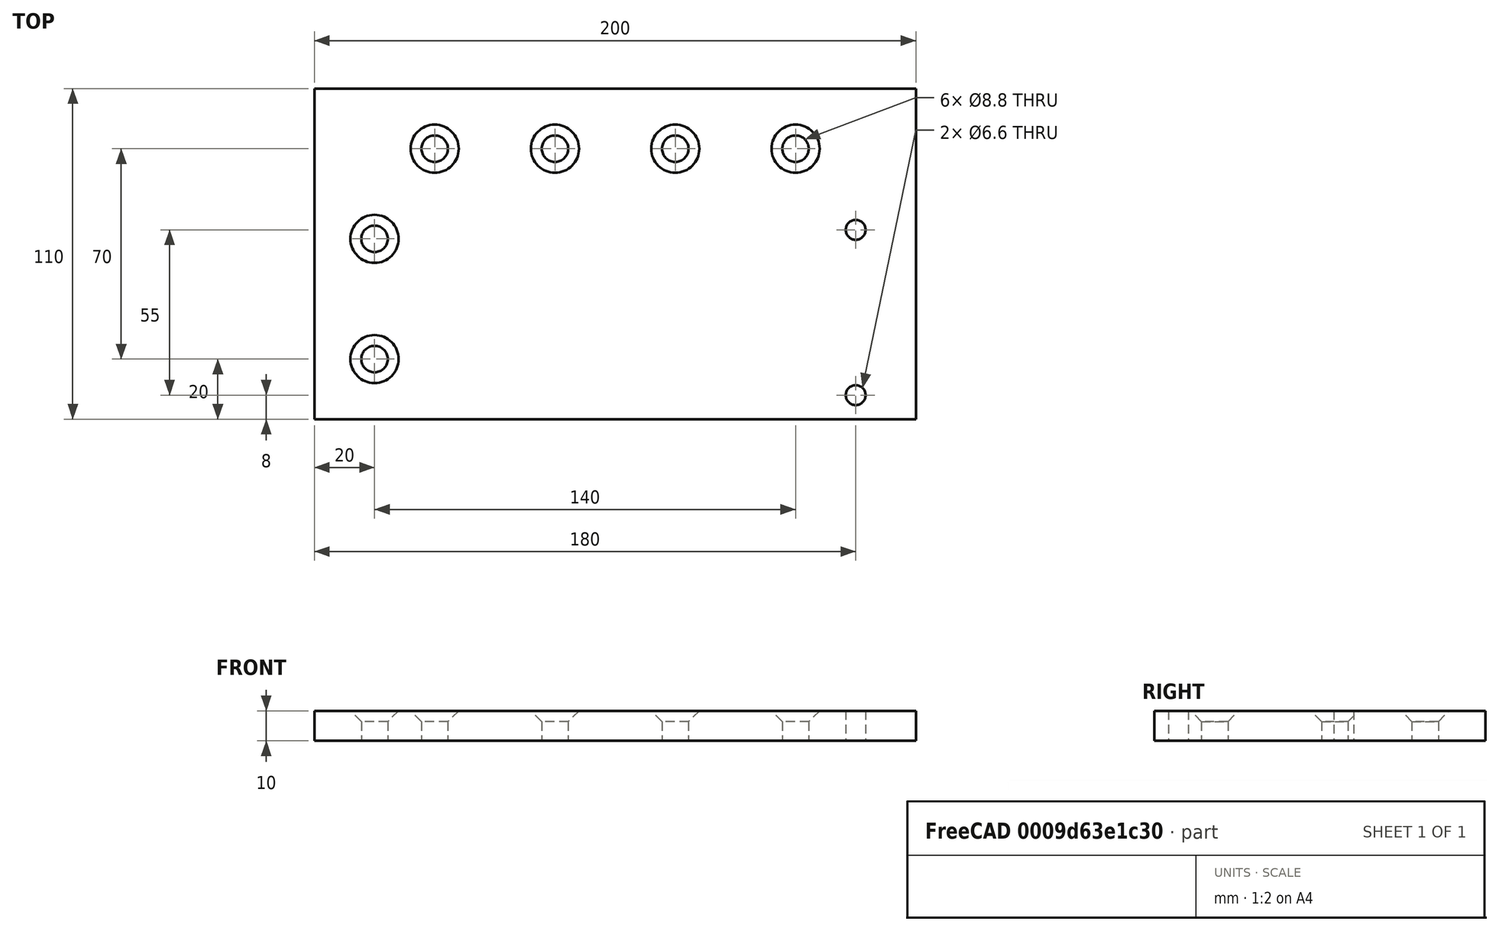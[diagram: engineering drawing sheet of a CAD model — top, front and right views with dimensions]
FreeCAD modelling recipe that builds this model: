
FCSTD DOCUMENT  (FreeCAD 0.17R13528 (Git))
Label: plate4
License: All rights reserved
LicenseURL: http://en.wikipedia.org/wiki/All_rights_reserved
objects: TechDraw::DrawViewDimension×22, Sketcher::SketchObject×4, PartDesign::Hole×3, PartDesign::LinearPattern×3, TechDraw::DrawProjGroupItem×3, PartDesign::Pad×1, PartDesign::Body×1, TechDraw::DrawSVGTemplate×1, TechDraw::DrawProjGroup×1, TechDraw::DrawViewAnnotation×1, TechDraw::DrawPage×1
note: 16 computed .brp shape members not serialized (recipe doc carries the construction recipe); baked Part::Feature solids carry a one-line shape summary decoded from their .brp

FEATURE [Sketcher::SketchObject] Sketch
  MapMode = 5
  Support = -> [XY_Plane]
  sketch-geometry (4):
    g0: LineSegment StartX=0 StartY=0 StartZ=0 EndX=200 EndY=0 EndZ=0
    g1: LineSegment StartX=200 StartY=0 StartZ=0 EndX=200 EndY=110 EndZ=0
    g2: LineSegment StartX=200 StartY=110 StartZ=0 EndX=0 EndY=110 EndZ=0
    g3: LineSegment StartX=0 StartY=110 StartZ=0 EndX=0 EndY=0 EndZ=0
  constraints (11):
    c: Coincident(g0,g1)
    c: Coincident(g1,g2)
    c: Coincident(g2,g3)
    c: Coincident(g3,g0)
    c: Horizontal(g0)
    c: Horizontal(g2)
    c: Vertical(g1)
    c: Vertical(g3)
    c: Coincident(g0,g-1)
    c: DistanceX(g0,g0) = 200
    c: DistanceY(g3,g3) = 110
FEATURE [PartDesign::Pad] Pad
  Length = 10
  Length2 = 100
  Profile = -> Sketch
  Type = 0
FEATURE [Sketcher::SketchObject] Sketch001
  MapMode = 5
  Placement = pos=(0,0,10) rot=(0,0,1;0rad)
  Support = -> [Pad]
  sketch-geometry (1):
    g0: Circle CenterX=20 CenterY=20 CenterZ=0 NormalX=0 NormalY=0 NormalZ=1 AngleXU=0 Radius=6.68651
  constraints (2):
    c: Distance(g0,g-1) = 20
    c: Distance(g0,g-2) = 20
FEATURE [PartDesign::Hole] Hole
  BaseFeature = -> Pad
  Depth = 25
  DepthType = 1
  Diameter = 8.8
  DrillPoint = 0
  DrillPointAngle = 118
  HoleCutCountersinkAngle = 90
  HoleCutDepth = 0
  HoleCutDiameter = 16
  HoleCutType = 2
  ModelActualThread = false
  Profile = -> Sketch001
  Tapered = false
  TaperedAngle = 90
  ThreadAngle = 0
  ThreadClass = 0
  ThreadCutOffInner = 0
  ThreadCutOffOuter = 0
  ThreadDirection = 0
  ThreadFit = 0
  ThreadPitch = 0
  ThreadSize = 8
  ThreadType = 1
  Threaded = false
FEATURE [PartDesign::LinearPattern] LinearPattern
  BaseFeature = -> Hole
  Direction = -> Sketch001 [V_Axis]
  Length = 40
  Occurrences = 2
  Originals = -> [Hole]
FEATURE [Sketcher::SketchObject] Sketch002
  MapMode = 5
  Placement = pos=(0,0,10) rot=(0,0,1;0rad)
  sketch-geometry (1):
    g0: Circle CenterX=180 CenterY=63 CenterZ=0 NormalX=0 NormalY=0 NormalZ=1 AngleXU=0 Radius=8.06203
  constraints (2):
    c: Distance(g0,g-1) = 63
    c: Distance(g0,g-2) = 180
FEATURE [PartDesign::Hole] Hole001
  BaseFeature = -> LinearPattern
  Depth = 25
  DepthType = 1
  Diameter = 6.6
  DrillPoint = 0
  DrillPointAngle = 118
  HoleCutCountersinkAngle = 90
  HoleCutDepth = 0
  HoleCutDiameter = 6
  HoleCutType = 0
  ModelActualThread = false
  Profile = -> Sketch002
  Tapered = false
  TaperedAngle = 90
  ThreadAngle = 60
  ThreadClass = 0
  ThreadCutOffInner = 0.108253
  ThreadCutOffOuter = 0.216506
  ThreadDirection = 1
  ThreadFit = 0
  ThreadPitch = 1
  ThreadSize = 7
  ThreadType = 1
  Threaded = false
FEATURE [PartDesign::LinearPattern] LinearPattern001
  BaseFeature = -> Hole001
  Direction = -> Sketch002 [V_Axis]
  Length = 55
  Occurrences = 2
  Originals = -> [Hole001]
  Reversed = true
FEATURE [Sketcher::SketchObject] Sketch003
  MapMode = 5
  Placement = pos=(0,0,10) rot=(0,0,1;0rad)
  Support = -> [LinearPattern001]
  sketch-geometry (1):
    g0: Circle CenterX=40 CenterY=90 CenterZ=0 NormalX=0 NormalY=0 NormalZ=1 AngleXU=0 Radius=9.62822
  constraints (2):
    c: Distance(g0,g-1) = 90
    c: Distance(g0,g-2) = 40
FEATURE [PartDesign::Hole] Hole002
  BaseFeature = -> LinearPattern001
  Depth = 25
  DepthType = 1
  Diameter = 8.8
  DrillPoint = 0
  DrillPointAngle = 118
  HoleCutCountersinkAngle = 90
  HoleCutDepth = 0
  HoleCutDiameter = 16
  HoleCutType = 2
  ModelActualThread = false
  Profile = -> Sketch003
  Tapered = false
  TaperedAngle = 90
  ThreadAngle = 0
  ThreadClass = 0
  ThreadCutOffInner = 0
  ThreadCutOffOuter = 0
  ThreadDirection = 0
  ThreadFit = 0
  ThreadPitch = 0
  ThreadSize = 8
  ThreadType = 1
  Threaded = false
FEATURE [PartDesign::LinearPattern] LinearPattern002
  BaseFeature = -> Hole002
  Direction = -> Sketch003 [H_Axis]
  Length = 120
  Occurrences = 4
  Originals = -> [Hole002]
FEATURE [PartDesign::Body] Body
  Group = -> [Sketch,Pad,Sketch001,Hole,LinearPattern,Sketch002,Hole001,LinearPattern001,Sketch003,Hole002,LinearPattern002]
  Origin = -> Origin
  Tip = -> LinearPattern002
FEATURE [TechDraw::DrawSVGTemplate] Template001
  EditableTexts = Designed_by_Name=Lukas Winter; FC-Date=27.08.2018; FC-SC=1:2; FC-SH=1/1; FC-Title=COSI Measure v1.0; Subtitle=Mechanical assembly - plate 4
  Height = 210
  Orientation = 1
  Width = 297
FEATURE [TechDraw::DrawProjGroupItem] ProjItem  label="Front"
  CoarseView = false
  Direction = (0,-1,0)
  Focus = 100
  HardHidden = false
  IsoCount = 0
  IsoHidden = false
  IsoVisible = false
  LockPosition = false
  Perspective = false
  Rotation = 0
  RotationVector = (1,0,0)
  ScaleType = 0
  SeamHidden = false
  SeamVisible = false
  SmoothHidden = false
  SmoothVisible = false
  Source = -> [Body]
  Type = 0
  X = 0
  Y = 87.5
FEATURE [TechDraw::DrawProjGroupItem] ProjItem001  label="Top"
  CoarseView = false
  Direction = (0,0,1)
  Focus = 100
  HardHidden = false
  IsoCount = 0
  IsoHidden = false
  IsoVisible = false
  LockPosition = false
  Perspective = false
  Rotation = 0
  RotationVector = (1,0,0)
  ScaleType = 0
  SeamHidden = false
  SeamVisible = false
  SmoothHidden = false
  SmoothVisible = false
  Source = -> [Body]
  Type = 4
  X = 0
  Y = -70
FEATURE [TechDraw::DrawProjGroupItem] ProjItem002  label="Left"
  CoarseView = false
  Direction = (-1,0,0)
  Focus = 100
  HardHidden = false
  IsoCount = 0
  IsoHidden = false
  IsoVisible = false
  LockPosition = false
  Perspective = false
  Rotation = 0
  RotationVector = (0,1,0)
  ScaleType = 0
  SeamHidden = false
  SeamVisible = false
  SmoothHidden = false
  SmoothVisible = false
  Source = -> [Body]
  Type = 1
  X = 115
  Y = 0
FEATURE [TechDraw::DrawProjGroup] ProjGroup
  Anchor = -> ProjItem
  AutoDistribute = true
  CubeDirs = (1) [(0,0,0)]
  CubeRotations = (1) [(0,0,0)]
  LockPosition = false
  ProjectionType = 0
  Rotation = 0
  Scale = 0.5
  ScaleType = 2
  Source = -> [Body]
  Views = -> [ProjItem,ProjItem001,ProjItem002]
  X = 87.5072
  Y = 170.793
  spacingX = 15
  spacingY = 15
FEATURE [TechDraw::DrawViewDimension] Dimension
  FormatSpec = %.2f
  LockPosition = false
  MeasureType = 1
  References2D = -> [ProjItem002]
  Rotation = 0
  ScaleType = 0
  Type = 2
  X = 53.2
  Y = -14.9333
FEATURE [TechDraw::DrawViewDimension] Dimension001
  FormatSpec = %.2f
  LockPosition = false
  MeasureType = 1
  References2D = -> [ProjItem002]
  Rotation = 0
  ScaleType = 0
  Type = 1
  X = 0
  Y = 14.3111
FEATURE [TechDraw::DrawViewDimension] Dimension002
  FormatSpec = %.2f
  LockPosition = false
  MeasureType = 1
  References2D = -> [ProjItem]
  Rotation = 0
  ScaleType = 0
  Type = 1
  X = 0.311111
  Y = 14.9333
FEATURE [TechDraw::DrawViewDimension] Dimension003
  FormatSpec = %.2f
  LockPosition = false
  MeasureType = 1
  References2D = -> [ProjItem001]
  Rotation = 0
  ScaleType = 0
  Type = 5
  X = 12.3494
  Y = -11.9086
FEATURE [TechDraw::DrawViewDimension] Dimension004
  FormatSpec = %.2f
  LockPosition = false
  MeasureType = 1
  References2D = -> [ProjItem001]
  Rotation = 0
  ScaleType = 0
  Type = 5
  X = 12.3494
  Y = -11.9086
FEATURE [TechDraw::DrawViewDimension] Dimension006
  FormatSpec = %.2f
  LockPosition = false
  MeasureType = 1
  References2D = -> [ProjItem001]
  Rotation = 0
  ScaleType = 0
  Type = 5
  X = -0.864198
  Y = 0.216049
FEATURE [TechDraw::DrawViewDimension] Dimension012
  FormatSpec = %.2f
  LockPosition = false
  MeasureType = 1
  References2D = -> [ProjItem001]
  Rotation = 0
  ScaleType = 0
  Type = 2
  X = -59.8776
  Y = -27.6904
FEATURE [TechDraw::DrawViewDimension] Dimension015
  FormatSpec = %.2f
  LockPosition = false
  MeasureType = 1
  References2D = -> [ProjItem001]
  Rotation = 0
  ScaleType = 0
  Type = 1
  X = 0.47334
  Y = 38.1039
FEATURE [TechDraw::DrawViewDimension] Dimension016
  FormatSpec = %.2f
  LockPosition = false
  MeasureType = 1
  References2D = -> [ProjItem001]
  Rotation = 0
  ScaleType = 0
  Type = 1
  X = 20.117
  Y = 38.1039
FEATURE [TechDraw::DrawViewDimension] Dimension017
  FormatSpec = %.2f
  LockPosition = false
  MeasureType = 1
  References2D = -> [ProjItem001]
  Rotation = 0
  ScaleType = 0
  Type = 1
  X = -40.45
  Y = 11.9619
FEATURE [TechDraw::DrawViewDimension] Dimension018
  FormatSpec = %.2f
  LockPosition = false
  MeasureType = 1
  References2D = -> [ProjItem001]
  Rotation = 0
  ScaleType = 0
  Type = 2
  X = 63.4276
  Y = -14.4369
FEATURE [TechDraw::DrawViewDimension] Dimension019
  FormatSpec = %.2f
  LockPosition = false
  MeasureType = 1
  References2D = -> [ProjItem001]
  Rotation = 0
  ScaleType = 0
  Type = 2
  X = 54.1975
  Y = -9.70348
FEATURE [TechDraw::DrawViewDimension] Dimension020
  FormatSpec = %.2f
  LockPosition = false
  MeasureType = 1
  References2D = -> [ProjItem001]
  Rotation = 0
  ScaleType = 0
  Type = 1
  X = 40.7073
  Y = 37.8672
FEATURE [TechDraw::DrawViewDimension] Dimension021
  FormatSpec = %.2f
  LockPosition = false
  MeasureType = 1
  References2D = -> [ProjItem001]
  Rotation = 0
  ScaleType = 0
  Type = 2
  X = 54.1975
  Y = 15.6202
FEATURE [TechDraw::DrawViewDimension] Dimension022
  FormatSpec = %.2f
  LockPosition = false
  MeasureType = 1
  References2D = -> [ProjItem001]
  Rotation = 0
  ScaleType = 0
  Type = 2
  X = -40.6609
  Y = 26.2067
FEATURE [TechDraw::DrawViewDimension] Dimension024
  FormatSpec = %.2f
  LockPosition = false
  MeasureType = 1
  References2D = -> [ProjItem001]
  Rotation = 0
  ScaleType = 0
  Type = 1
  X = -42.0557
  Y = -44.8408
FEATURE [TechDraw::DrawViewDimension] Dimension025
  FormatSpec = %.2f
  LockPosition = false
  MeasureType = 1
  References2D = -> [ProjItem001]
  Rotation = 0
  ScaleType = 0
  Type = 1
  X = 48.7246
  Y = -41.4465
FEATURE [TechDraw::DrawViewDimension] Dimension026
  FormatSpec = %.2f
  LockPosition = false
  MeasureType = 1
  References2D = -> [ProjItem001]
  Rotation = 0
  ScaleType = 0
  Type = 5
  X = 9.50617
  Y = 4.75309
FEATURE [TechDraw::DrawViewAnnotation] Annotation
  Font = osifont
  LineSpace = 80
  LockPosition = false
  MaxWidth = -1
  Rotation = 0
  ScaleType = 0
  Text = Make a countersink in the d=8.8mm holes.
  TextSize = 4
  TextStyle = 0
  X = 237.08
  Y = 72.5926
FEATURE [TechDraw::DrawViewDimension] Dimension027
  FormatSpec = %.2f
  LockPosition = false
  MeasureType = 1
  References2D = -> [ProjItem001]
  Rotation = 0
  ScaleType = 0
  Type = 1
  X = -37.5926
  Y = 38.0247
FEATURE [TechDraw::DrawViewDimension] Dimension028
  FormatSpec = %.2f
  LockPosition = false
  MeasureType = 1
  References2D = -> [ProjItem001]
  Rotation = 0
  ScaleType = 0
  Type = 1
  X = -17.9321
  Y = 38.0247
FEATURE [TechDraw::DrawViewDimension] Dimension029
  FormatSpec = %.2f
  LockPosition = false
  MeasureType = 1
  References2D = -> [ProjItem001]
  Rotation = 0
  ScaleType = 0
  Type = 2
  X = -70.6481
  Y = -7.34568
FEATURE [TechDraw::DrawViewDimension] Dimension030
  FormatSpec = %.2f
  LockPosition = false
  MeasureType = 1
  References2D = -> [ProjItem001]
  Rotation = 0
  ScaleType = 0
  Type = 2
  X = -70.6481
  Y = 13.3951
FEATURE [TechDraw::DrawPage] Page001
  KeepUpdated = true
  ProjectionType = 0
  Template = -> Template001
  Views = -> [ProjGroup,Dimension,Dimension001,Dimension002,Dimension003,Dimension004,Dimension006,Dimension012,Dimension015,Dimension016,Dimension017,Dimension018,Dimension019,Dimension020,Dimension021,Dimension022,Dimension024,Dimension025,Dimension026,Annotation,Dimension027,Dimension028,Dimension029,Dimension030]
